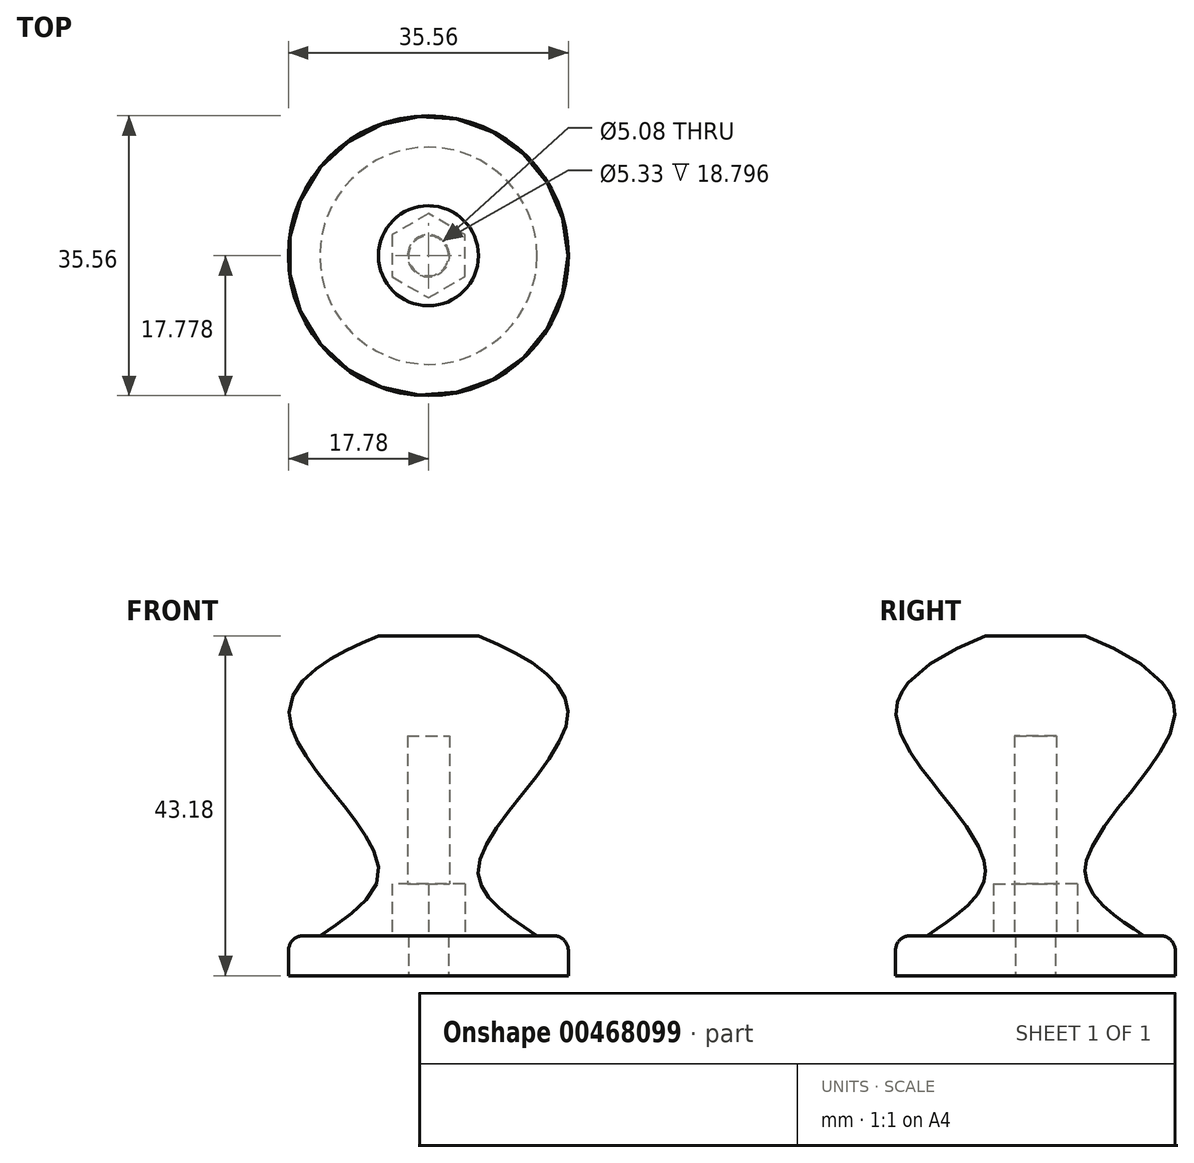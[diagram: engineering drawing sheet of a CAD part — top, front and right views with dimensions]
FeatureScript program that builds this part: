
annotation { "Feature Type Name" : "Feature", "Feature Type Description" : "" }
export const myFeature = defineFeature(function(context is Context, id is Id, definition is map)
    precondition{}
    {
        {
            var Q0;
            Q0=qCreatedBy(makeId("Right.planeOp"),FACE);
            var sketch = newSketch(context, id + "F0", { "sketchPlane" : qUnion([Q0])});
            skLineSegment(sketch, "E0", {"start": v(-17.65, 45.29) * mm, "end": v(-17.65, 7.19) * mm});
            skLineSegment(sketch, "E1", {"start": v(-17.65, 45.29) * mm, "end": v(-11.3, 45.29) * mm});
            skFitSpline(sketch, "E2", {"points": [v(-11.3, 45.29) * mm, v(0, 34.69) * mm, v(-11.3, 15.95) * mm, v(-3.86, 7.19) * mm], "startDerivative": vector(57.76, -23.9) * mm, "endDerivative": vector(36.9, -25.45) * mm});
            skLineSegment(sketch, "E3", {"start": v(-17.65, 7.19) * mm, "end": v(-3.86, 7.19) * mm});
            skSolve(sketch);
        }
        {
            var Q0;
            Q0=makeQuery(id+"F0.imprint","IMPRINT",FACE,{"disambiguationData":[TD([[makeQuery(id+"F0.imprint","IMPRINT",EDGE,{"derivedFrom":sQuery(id+"F0.wireOp",EDGE,"E0")}),1.0]])]});
            var Q1;
            Q1=sQuery(id+"F0.wireOp",EDGE,"E0");
            revolve(context, id + "F1", {"entities" : qUnion([Q0]), "axis" : qUnion([Q1]), "revolveType" : RevolveType.FULL});
        }
        {
            var Q0;
            Q0=makeQuery(id+"F1.opRevolve","SWEPT_FACE",FACE,{"disambiguationData":[OSD([sQuery(id+"F0.wireOp",EDGE,"E3")])]});
            var sketch = newSketch(context, id + "F2", { "sketchPlane" : qUnion([Q0])});
            skCircle(sketch, "E4", {"center": v(0, 17.65) * mm, "radius": 2.67 * mm});
            skSolve(sketch);
        }
        {
            var Q0;
            Q0 = qSketchRegion(id + "F2", true);
            extrude(context, id + "F3", {"entities" : qUnion([Q0]), "operationType" : NewBodyOperationType.ADD, "oppositeDirection" : true, "depth" : 25.4 * mm});
        }
        {
            var Q0;
            Q0=makeQuery(id+"F1.opRevolve","SWEPT_FACE",FACE,{"disambiguationData":[OSD([sQuery(id+"F0.wireOp",EDGE,"E3")])]});
            var sketch = newSketch(context, id + "F4", { "sketchPlane" : qUnion([Q0])});
            skCircle(sketch, "E5", {"center": v(0, 17.65) * mm, "radius": 2.67 * mm});
            skSolve(sketch);
        }
        {
            var Q0;
            Q0 = qSketchRegion(id + "F4", true);
            extrude(context, id + "F5", {"entities" : qUnion([Q0]), "operationType" : NewBodyOperationType.ADD, "oppositeDirection" : true, "depth" : 25.65 * mm});
        }
        {
            var Q0;
            Q0 = qSketchRegion(id + "F4", true);
            extrude(context, id + "F6", {"entities" : qUnion([Q0]), "operationType" : NewBodyOperationType.REMOVE, "oppositeDirection" : true, "depth" : 25.4 * mm});
        }
        {
            var Q0;
            Q0=makeQuery(id+"F1.opRevolve","SWEPT_FACE",FACE,{"disambiguationData":[OSD([sQuery(id+"F0.wireOp",EDGE,"E3")])]});
            var sketch = newSketch(context, id + "F7", { "sketchPlane" : qUnion([Q0])});
            skCircle(sketch, "E6.cCircle", {"center": v(0, 17.65) * mm, "radius": 4.62 * mm, "construction": true});
            skLineSegment(sketch, "E6.0", {"start": v(-4.62, 14.98) * mm, "end": v(-4.62, 20.32) * mm});
            skLineSegment(sketch, "E6.1", {"start": v(-4.62, 20.32) * mm, "end": v(0, 22.99) * mm});
            skLineSegment(sketch, "E6.2", {"start": v(0, 22.99) * mm, "end": v(4.62, 20.32) * mm});
            skLineSegment(sketch, "E6.3", {"start": v(4.62, 20.32) * mm, "end": v(4.62, 14.98) * mm});
            skLineSegment(sketch, "E6.4", {"start": v(4.62, 14.98) * mm, "end": v(0, 12.32) * mm});
            skLineSegment(sketch, "E6.5", {"start": v(0, 12.32) * mm, "end": v(-4.62, 14.98) * mm});
            skPoint(sketch, "E6.0.midPoint", {"position": v(-4.62, 17.65) * mm});
            skSolve(sketch);
        }
        {
            var Q0;
            Q0 = qSketchRegion(id + "F7", true);
            extrude(context, id + "F8", {"entities" : qUnion([Q0]), "operationType" : NewBodyOperationType.REMOVE, "oppositeDirection" : true, "depth" : 6.6 * mm});
        }
        {
            var Q0;
            Q0=makeQuery(id+"F1.opRevolve","SWEPT_FACE",FACE,{"disambiguationData":[OSD([sQuery(id+"F0.wireOp",EDGE,"E3")])]});
            var sketch = newSketch(context, id + "F9", { "sketchPlane" : qUnion([Q0])});
            skCircle(sketch, "E7", {"center": v(0, 17.65) * mm, "radius": 17.78 * mm});
            skSolve(sketch);
        }
        {
            var Q0;
            Q0 = qSketchRegion(id + "F9", true);
            extrude(context, id + "F10", {"entities" : qUnion([Q0]), "operationType" : NewBodyOperationType.ADD, "depth" : 5.08 * mm});
        }
        {
            var Q0;
            Q0=makeQuery(id+"F10.opExtrude","CAP_FACE",FACE,{"disambiguationData":[OSD([sQuery(id+"F9.wireOp",EDGE,"E7")])],"isStart":false});
            var sketch = newSketch(context, id + "F11", { "sketchPlane" : qUnion([Q0])});
            skCircle(sketch, "E8", {"center": v(0, 17.65) * mm, "radius": 2.54 * mm});
            skSolve(sketch);
        }
        {
            var Q0;
            Q0=makeQuery(id+"F11.imprint","IMPRINT",FACE,{"disambiguationData":[TD([[makeQuery(id+"F11.imprint","IMPRINT",EDGE,{"derivedFrom":sQuery(id+"F11.wireOp",EDGE,"E8")}),1.0]])]});
            var Q1;
            Q1=sQuery(id+"F11.wireOp",EDGE,"E8");
            extrude(context, id + "F12", {"entities" : qUnion([Q0]), "operationType" : NewBodyOperationType.REMOVE, "surfaceEntities" : qUnion([Q1]), "endBound" : BoundingType.UP_TO_NEXT, "oppositeDirection" : true, "depth" : 25.4 * mm, "hasSecondDirection" : true, "secondDirectionOppositeDirection" : false, "secondDirectionDepth" : 25.4 * mm});
        }
        {
            var Q0;
            Q0=makeQuery(id+"F10.opExtrude","CAP_EDGE",EDGE,{"disambiguationData":[OSD([sQuery(id+"F9.wireOp",EDGE,"E7")])],"isStart":true});
            fillet(context, id + "F13", {"entities" : qUnion([Q0]), "radius" : 1.9 * mm, "tangentPropagation" : true, "allowEdgeOverflow" : false});
        }
    });
